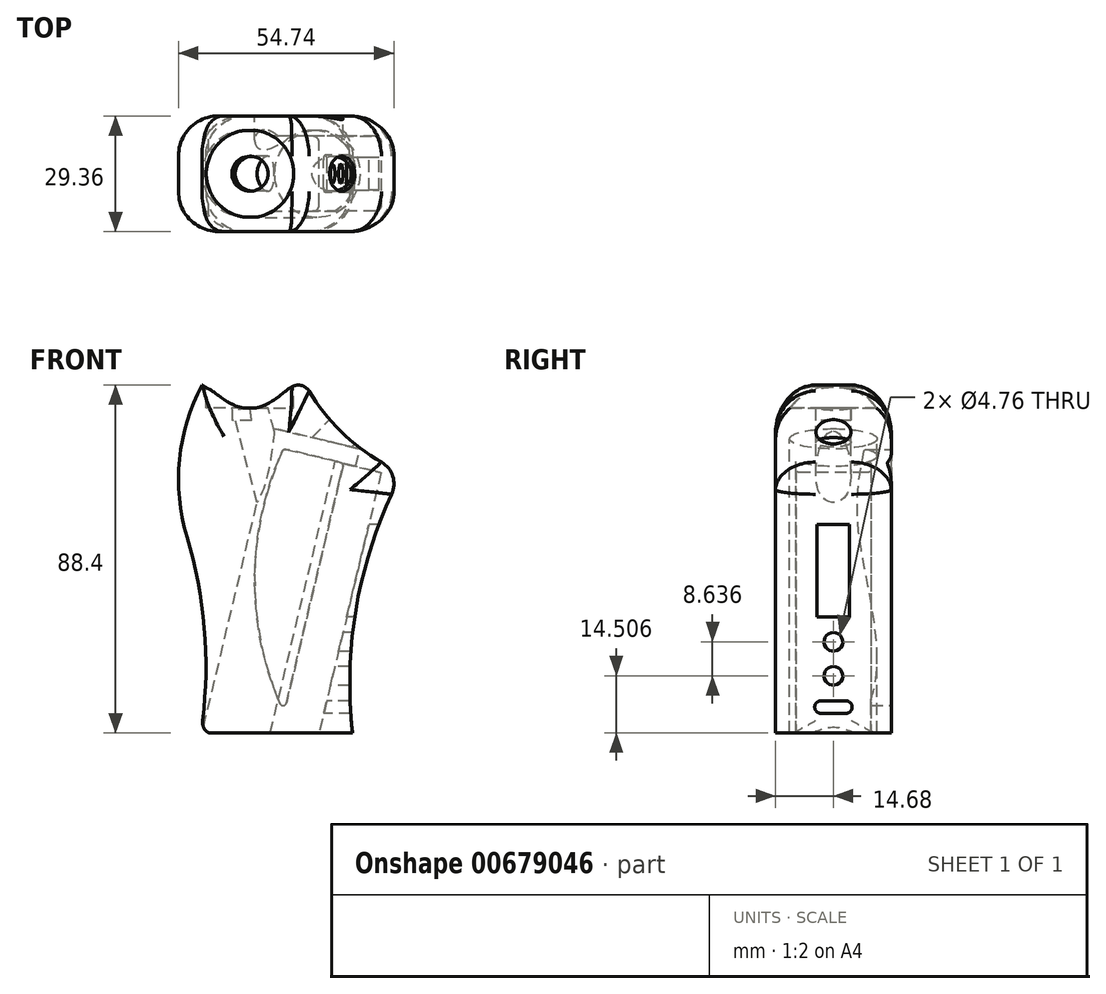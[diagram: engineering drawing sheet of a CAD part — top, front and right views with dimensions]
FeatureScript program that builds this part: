
annotation { "Feature Type Name" : "Feature", "Feature Type Description" : "" }
export const myFeature = defineFeature(function(context is Context, id is Id, definition is map)
    precondition{}
    {
        {
            var Q0;
            Q0=qCreatedBy(makeId("Front.planeOp"),FACE);
            var sketch = newSketch(context, id + "F0", { "sketchPlane" : qUnion([Q0])});
            skLineSegment(sketch, "E0", {"start": v(-23.81, -66.17) * mm, "end": v(12.7, -66.17) * mm});
            skArc(sketch, "E1", {"start": v(22.65, -5.53) * mm, "mid": v(13.52, -35.17) * mm, "end": v(12.7, -66.17) * mm});
            skArc(sketch, "E2", {"start": v(1.68, 20.68) * mm, "mid": v(9.7, 10.49) * mm, "end": v(20.04, 2.66) * mm});
            skArc(sketch, "E3", {"start": v(-25.38, -63.03) * mm, "mid": v(-24.94, -39.47) * mm, "end": v(-29.35, -16.32) * mm});
            skArc(sketch, "E4", {"start": v(-25.5, 22.23) * mm, "mid": v(-31.24, 3.33) * mm, "end": v(-29.35, -16.32) * mm});
            skLineSegment(sketch, "E5", {"start": v(23.15, -3.9) * mm, "end": v(12.7, -66.17) * mm, "construction": true});
            skLineSegment(sketch, "E6", {"start": v(-31.5, 18.67) * mm, "end": v(-31.5, -66.17) * mm, "construction": true});
            skPoint(sketch, "E7.visualSharp", {"position": v(25.4, 0) * mm});
            skArc(sketch, "E7.filletArc", {"start": v(22.65, -5.53) * mm, "mid": v(22.94, -0.93) * mm, "end": v(20.04, 2.66) * mm});
            skLineSegment(sketch, "E8", {"start": v(23.24, 22.23) * mm, "end": v(23.24, -66.17) * mm, "construction": true});
            skLineSegment(sketch, "E9", {"start": v(-33.86, 18.67) * mm, "end": v(-25.13, -66.17) * mm, "construction": true});
            skPoint(sketch, "E10.visualSharp", {"position": v(0, 23.71) * mm});
            skArc(sketch, "E11", {"start": v(-25.5, 22.23) * mm, "mid": v(-14.17, 18.67) * mm, "end": v(-2.7, 21.76) * mm});
            skLineSegment(sketch, "E12", {"start": v(-33.86, 18.67) * mm, "end": v(23.24, 18.67) * mm, "construction": true});
            skArc(sketch, "E13.filletArc", {"start": v(1.68, 20.68) * mm, "mid": v(-0.29, 22.13) * mm, "end": v(-2.7, 21.76) * mm});
            skLineSegment(sketch, "E14", {"start": v(-25.5, 22.23) * mm, "end": v(23.24, 22.23) * mm, "construction": true});
            skArc(sketch, "E15", {"start": v(-25.38, -63.03) * mm, "mid": v(-25.07, -64.83) * mm, "end": v(-23.81, -66.17) * mm});
            skLineSegment(sketch, "E16", {"start": v(-25.4, 18.67) * mm, "end": v(-25.4, -66.17) * mm, "construction": true});
            skLineSegment(sketch, "E17", {"start": v(0.24, 22.23) * mm, "end": v(23.24, -0.17) * mm, "construction": true});
            skSolve(sketch);
        }
        {
            var Q0;
            Q0=makeQuery(id+"F0.imprint","IMPRINT",FACE,{"disambiguationData":[TD([[makeQuery(id+"F0.imprint","IMPRINT",EDGE,{"derivedFrom":sQuery(id+"F0.wireOp",EDGE,"E0")}),1.0]])]});
            extrude(context, id + "F1", {"entities" : qUnion([Q0]), "endBound" : BoundingType.SYMMETRIC, "depth" : 29.37 * mm, "offsetDistance" : 25.4 * mm});
        }
        {
            var Q0;
            Q0=makeQuery(id+"F1.opExtrude","CAP_EDGE",EDGE,{"disambiguationData":[OSD([sQuery(id+"F0.wireOp",EDGE,"8a65d561-aca7-42f6-96eb-58d541bab6f2")])],"isStart":true});
            var Q1;
            Q1=makeQuery(id+"F1.opExtrude","CAP_EDGE",EDGE,{"disambiguationData":[OSD([sQuery(id+"F0.wireOp",EDGE,"E2")])],"isStart":true});
            var Q2;
            Q2=makeQuery(id+"F1.opExtrude","CAP_EDGE",EDGE,{"disambiguationData":[OSD([sQuery(id+"F0.wireOp",EDGE,"E2")])],"isStart":false});
            var Q3;
            Q3=makeQuery(id+"F1.opExtrude","CAP_EDGE",EDGE,{"disambiguationData":[OSD([sQuery(id+"F0.wireOp",EDGE,"E1")])],"isStart":false});
            var Q4;
            Q4=makeQuery(id+"F1.opExtrude","CAP_EDGE",EDGE,{"disambiguationData":[OSD([sQuery(id+"F0.wireOp",EDGE,"E1")])],"isStart":true});
            var Q5;
            Q5=makeQuery(id+"F1.opExtrude","CAP_EDGE",EDGE,{"disambiguationData":[OSD([sQuery(id+"F0.wireOp",EDGE,"E3")])],"isStart":false});
            var Q6;
            Q6=makeQuery(id+"F1.opExtrude","CAP_EDGE",EDGE,{"disambiguationData":[OSD([sQuery(id+"F0.wireOp",EDGE,"E4")])],"isStart":false});
            var Q7;
            Q7=makeQuery(id+"F1.opExtrude","CAP_EDGE",EDGE,{"disambiguationData":[OSD([sQuery(id+"F0.wireOp",EDGE,"E4")])],"isStart":true});
            var Q8;
            Q8=makeQuery(id+"F1.opExtrude","CAP_EDGE",EDGE,{"disambiguationData":[OSD([sQuery(id+"F0.wireOp",EDGE,"E3")])],"isStart":true});
            var Q9;
            Q9=makeQuery(id+"F1.opExtrude","CAP_EDGE",EDGE,{"disambiguationData":[OSD([sQuery(id+"F0.wireOp",EDGE,"8a65d561-aca7-42f6-96eb-58d541bab6f2")])],"isStart":false});
            var Q10;
            Q10=makeQuery(id+"F1.opExtrude","CAP_EDGE",EDGE,{"disambiguationData":[OSD([sQuery(id+"F0.wireOp",EDGE,"E7.filletArc")])],"isStart":false});
            var Q11;
            Q11=makeQuery(id+"F1.opExtrude","CAP_EDGE",EDGE,{"disambiguationData":[OSD([sQuery(id+"F0.wireOp",EDGE,"E7.filletArc")])],"isStart":true});
            fillet(context, id + "F2", {"entities" : qUnion([Q0, Q1, Q2, Q3, Q4, Q5, Q6, Q7, Q8, Q9, Q10, Q11]), "radius" : 10.16 * mm, "tangentPropagation" : true, "allowEdgeOverflow" : false});
        }
        {
            var Q0;
            Q0=qCreatedBy(makeId("Top.planeOp"),FACE);
            cPlane(context, id + "F3", {"entities" : qUnion([Q0]), "cplaneType" : CPlaneType.OFFSET, "offset" : 22.22 * mm, "width" : 152.4 * mm, "height" : 152.4 * mm});
        }
        {
            var Q0;
            Q0=qCreatedBy(id+"F3.planeOp",FACE);
            var sketch = newSketch(context, id + "F4", { "sketchPlane" : qUnion([Q0])});
            skCircle(sketch, "E18", {"center": v(-13.34, 0) * mm, "radius": 11.11 * mm});
            skSolve(sketch);
        }
        {
            var Q0;
            Q0 = qSketchRegion(id + "F4", true);
            extrude(context, id + "F5", {"entities" : qUnion([Q0]), "operationType" : NewBodyOperationType.REMOVE, "oppositeDirection" : true, "depth" : 5.84 * mm, "offsetDistance" : 25.4 * mm});
        }
        {
            var Q0;
            Q0=makeQuery(id+"F1.opExtrude","SWEPT_FACE",FACE,{"disambiguationData":[OSD([sQuery(id+"F0.wireOp",EDGE,"E0")])]});
            var sketch = newSketch(context, id + "F6", { "sketchPlane" : qUnion([Q0])});
            skCircle(sketch, "E19.0", {"center": v(-13.34, 0) * mm, "radius": 11.11 * mm});
            skSolve(sketch);
        }
        {
            var Q0;
            Q0=makeQuery(id+"F1.opExtrude","CAP_FACE",FACE,{"disambiguationData":[OSD([sQuery(id+"F0.wireOp",EDGE,"E0"),sQuery(id+"F0.wireOp",EDGE,"E1"),sQuery(id+"F0.wireOp",EDGE,"E2"),sQuery(id+"F0.wireOp",EDGE,"E3"),sQuery(id+"F0.wireOp",EDGE,"E4"),sQuery(id+"F0.wireOp",EDGE,"E7.filletArc"),sQuery(id+"F0.wireOp",EDGE,"E11"),sQuery(id+"F0.wireOp",EDGE,"E13.filletArc"),sQuery(id+"F0.wireOp",EDGE,"E15")])],"isStart":true});
            var sketch = newSketch(context, id + "F7", { "sketchPlane" : qUnion([Q0])});
            skLineSegment(sketch, "E20", {"start": v(4.06, -58.5) * mm, "end": v(-10.26, 1.52) * mm});
            skLineSegment(sketch, "E21", {"start": v(-9.59, 2.6) * mm, "end": v(4.11, 5.87) * mm});
            skArc(sketch, "E22", {"start": v(5.77, -58.64) * mm, "mid": v(12.13, -26.57) * mm, "end": v(5.15, 5.36) * mm});
            skLineSegment(sketch, "E23", {"start": v(0, 0) * mm, "end": v(0, -91.95) * mm, "construction": true});
            skPoint(sketch, "E24.visualSharp", {"position": v(4.68, -61.09) * mm});
            skArc(sketch, "E24.filletArc", {"start": v(4.06, -58.5) * mm, "mid": v(4.87, -59.18) * mm, "end": v(5.77, -58.64) * mm});
            skPoint(sketch, "E25.visualSharp", {"position": v(-10.46, 2.4) * mm});
            skArc(sketch, "E25.filletArc", {"start": v(-9.59, 2.6) * mm, "mid": v(-10.15, 2.2) * mm, "end": v(-10.26, 1.52) * mm});
            skPoint(sketch, "E26.visualSharp", {"position": v(4.84, 6.05) * mm});
            skArc(sketch, "E26.filletArc", {"start": v(5.15, 5.36) * mm, "mid": v(4.72, 5.8) * mm, "end": v(4.11, 5.87) * mm});
            skArc(sketch, "E27.0", {"start": v(-22.65, -5.53) * mm, "mid": v(-22.94, -0.93) * mm, "end": v(-20.04, 2.66) * mm});
            skSolve(sketch);
        }
        {
            var Q0;
            Q0 = qSketchRegion(id + "F7", true);
            var Q1;
            Q1=qCreatedBy(makeId("Front.planeOp"),FACE);
            extrude(context, id + "F8", {"entities" : qUnion([Q0]), "operationType" : NewBodyOperationType.REMOVE, "endBound" : BoundingType.UP_TO_SURFACE, "oppositeDirection" : true, "depth" : 25.4 * mm, "endBoundEntityFace" : qUnion([Q1]), "offsetDistance" : 25.4 * mm});
        }
        {
            var Q0;
            Q0=makeQuery(id+"F8.boolean.opBoolean","COPY",FACE,{"derivedFrom":makeQuery(id+"F8.opExtrude","SWEPT_FACE",FACE,{"disambiguationData":[OSD([sQuery(id+"F7.wireOp",EDGE,"E21")])]})});
            var sketch = newSketch(context, id + "F9", { "sketchPlane" : qUnion([Q0])});
            skCircle(sketch, "E28", {"center": v(1.68, 0) * mm, "radius": 11.11 * mm});
            skSolve(sketch);
        }
        {
            var Q0;
            Q0 = qSketchRegion(id + "F9", true);
            var Q1;
            Q1=makeQuery(id+"F1.opExtrude","SWEPT_FACE",FACE,{"disambiguationData":[OSD([sQuery(id+"F0.wireOp",EDGE,"E0")])]});
            extrude(context, id + "F10", {"entities" : qUnion([Q0]), "operationType" : NewBodyOperationType.REMOVE, "endBound" : BoundingType.UP_TO_SURFACE, "depth" : 25.4 * mm, "endBoundEntityFace" : qUnion([Q1]), "offsetDistance" : 25.4 * mm, "hasSecondDirection" : true, "secondDirectionOppositeDirection" : true, "secondDirectionDepth" : 4.44 * mm});
        }
        {
            var Q0;
            Q0=makeQuery(id+"F10.boolean.opBoolean","COPY",FACE,{"derivedFrom":makeQuery(id+"F10.opExtrude","CAP_FACE",FACE,{"disambiguationData":[OSD([sQuery(id+"F9.wireOp",EDGE,"E28")])],"isStart":true})});
            cPlane(context, id + "F11", {"entities" : qUnion([Q0]), "cplaneType" : CPlaneType.OFFSET, "offset" : 76.2 * mm, "flipAlignment" : true, "width" : 152.4 * mm, "height" : 152.4 * mm});
        }
        {
            var Q0;
            Q0=qCreatedBy(id+"F11.planeOp",FACE);
            var sketch = newSketch(context, id + "F12", { "sketchPlane" : qUnion([Q0])});
            skLineSegment(sketch, "E29", {"start": v(19.46, -7.94) * mm, "end": v(19.46, 7.94) * mm});
            skLineSegment(sketch, "E30", {"start": v(17.87, 9.53) * mm, "end": v(6.76, 9.53) * mm});
            skLineSegment(sketch, "E31", {"start": v(6.76, 9.53) * mm, "end": v(6.76, -9.52) * mm});
            skLineSegment(sketch, "E32", {"start": v(6.76, -9.52) * mm, "end": v(17.87, -9.52) * mm});
            skArc(sketch, "E33.0", {"start": v(-7.8, 5.8) * mm, "mid": v(12.8, 0) * mm, "end": v(-7.8, -5.8) * mm});
            skPoint(sketch, "E34.visualSharp", {"position": v(19.46, -9.52) * mm});
            skArc(sketch, "E34.filletArc", {"start": v(17.87, -9.52) * mm, "mid": v(19, -9.06) * mm, "end": v(19.46, -7.94) * mm});
            skPoint(sketch, "E35.visualSharp", {"position": v(19.46, 9.53) * mm});
            skArc(sketch, "E35.filletArc", {"start": v(19.46, 7.94) * mm, "mid": v(19, 9.06) * mm, "end": v(17.87, 9.53) * mm});
            skSolve(sketch);
        }
        {
            var Q0;
            Q0 = qSketchRegion(id + "F12", true);
            extrude(context, id + "F13", {"entities" : qUnion([Q0]), "operationType" : NewBodyOperationType.REMOVE, "oppositeDirection" : true, "depth" : 71.63 * mm, "offsetDistance" : 25.4 * mm});
        }
        {
            var Q0;
            Q0=qCreatedBy(makeId("Right.planeOp"),FACE);
            var sketch = newSketch(context, id + "F14", { "sketchPlane" : qUnion([Q0])});
            skLineSegment(sketch, "E36", {"start": v(-3.17, -59.6) * mm, "end": v(3.18, -59.6) * mm, "construction": true});
            skArc(sketch, "E37", {"start": v(-3.17, -58.01) * mm, "mid": v(-4.76, -59.6) * mm, "end": v(-3.17, -61.19) * mm});
            skArc(sketch, "E38", {"start": v(3.18, -61.19) * mm, "mid": v(4.76, -59.6) * mm, "end": v(3.18, -58.01) * mm});
            skLineSegment(sketch, "E39", {"start": v(-3.17, -58.01) * mm, "end": v(3.18, -58.01) * mm});
            skLineSegment(sketch, "E40", {"start": v(3.18, -61.19) * mm, "end": v(-3.17, -61.19) * mm});
            skLineSegment(sketch, "E41.0.0", {"start": v(-5.8, -66.17) * mm, "end": v(-11.11, -66.17) * mm});
            skLineSegment(sketch, "E41.0.2", {"start": v(7.94, -66.17) * mm, "end": v(7.94, -66.17) * mm});
            skLineSegment(sketch, "E41.0.4", {"start": v(11.11, -66.17) * mm, "end": v(5.8, -66.17) * mm});
            skLineSegment(sketch, "E41.0.5", {"start": v(5.8, -66.17) * mm, "end": v(10.54, -66.17) * mm});
            skFitSpline(sketch, "E41.0.6", {"points": [v(10.54, -66.17) * mm, v(11.92, -66.17) * mm, v(13.3, -66.17) * mm, v(14.68, -66.17) * mm]});
            skFitSpline(sketch, "E41.0.8", {"points": [v(14.68, -66.17) * mm, v(11.3, -66.17) * mm, v(7.91, -66.17) * mm, v(4.52, -66.17) * mm]});
            skLineSegment(sketch, "E41.0.9", {"start": v(4.52, -66.17) * mm, "end": v(-4.52, -66.17) * mm});
            skFitSpline(sketch, "E41.0.10", {"points": [v(-4.52, -66.17) * mm, v(-7.91, -66.17) * mm, v(-11.3, -66.17) * mm, v(-14.68, -66.17) * mm]});
            skFitSpline(sketch, "E41.0.12", {"points": [v(-14.68, -66.17) * mm, v(-13.3, -66.17) * mm, v(-11.92, -66.17) * mm, v(-10.54, -66.17) * mm]});
            skLineSegment(sketch, "E41.0.13", {"start": v(-10.54, -66.17) * mm, "end": v(-5.8, -66.17) * mm});
            skLineSegment(sketch, "E42", {"start": v(0, 0) * mm, "end": v(0, -80.2) * mm, "construction": true});
            skCircle(sketch, "E43", {"center": v(0, -51.66) * mm, "radius": 2.38 * mm});
            skCircle(sketch, "E44", {"center": v(0, -43.03) * mm, "radius": 2.38 * mm});
            skLineSegment(sketch, "E45", {"start": v(-4.13, -13.18) * mm, "end": v(-4.13, -36.68) * mm});
            skLineSegment(sketch, "E46", {"start": v(-4.13, -36.68) * mm, "end": v(4.13, -36.68) * mm});
            skLineSegment(sketch, "E47", {"start": v(4.13, -36.68) * mm, "end": v(4.13, -13.18) * mm});
            skLineSegment(sketch, "E48", {"start": v(4.13, -13.18) * mm, "end": v(-4.13, -13.18) * mm});
            skSolve(sketch);
        }
        {
            var Q0;
            Q0 = qSketchRegion(id + "F14", true);
            extrude(context, id + "F15", {"entities" : qUnion([Q0]), "operationType" : NewBodyOperationType.REMOVE, "endBound" : BoundingType.THROUGH_ALL, "depth" : 25.4 * mm, "offsetDistance" : 25.4 * mm});
        }
        {
            var Q0;
            Q0=sQuery(id+"F0.wireOp",EDGE,"E17");
            cPlane(context, id + "F16", {"entities" : qUnion([Q0]), "cplaneType" : CPlaneType.LINE_ANGLE, "offset" : 25.4 * mm, "angle" : 90 * degree, "width" : 152.4 * mm, "height" : 152.4 * mm});
        }
        {
            var Q0;
            Q0=qCreatedBy(id+"F16.planeOp",FACE);
            var sketch = newSketch(context, id + "F17", { "sketchPlane" : qUnion([Q0])});
            skCircle(sketch, "E49", {"center": v(0, 0) * mm, "radius": 4.45 * mm});
            skSolve(sketch);
        }
        {
            var Q0;
            Q0 = qSketchRegion(id + "F17", true);
            extrude(context, id + "F18", {"entities" : qUnion([Q0]), "operationType" : NewBodyOperationType.REMOVE, "oppositeDirection" : true, "depth" : 25.4 * mm, "offsetDistance" : 25.4 * mm});
        }
        {
            var Q0;
            Q0=qCreatedBy(makeId("Front.planeOp"),FACE);
            var sketch = newSketch(context, id + "F19", { "sketchPlane" : qUnion([Q0])});
            skLineSegment(sketch, "E50", {"start": v(14.58, 5.98) * mm, "end": v(13.52, 1.54) * mm});
            skLineSegment(sketch, "E51", {"start": v(-25.13, -64.69) * mm, "end": v(-7.04, 11.14) * mm});
            skLineSegment(sketch, "E52.0.0", {"start": v(4.22, -66.17) * mm, "end": v(20, -0.01) * mm});
            skLineSegment(sketch, "E52.0.1", {"start": v(20, -0.01) * mm, "end": v(10, 2.37) * mm});
            skArc(sketch, "E52.0.2", {"start": v(10.26, 1.52) * mm, "mid": v(10.24, 1.98) * mm, "end": v(10, 2.37) * mm});
            skLineSegment(sketch, "E52.0.3", {"start": v(10.26, 1.52) * mm, "end": v(-4.06, -58.5) * mm});
            skArc(sketch, "E52.0.4", {"start": v(-5.77, -58.64) * mm, "mid": v(-4.87, -59.18) * mm, "end": v(-4.06, -58.5) * mm});
            skArc(sketch, "E52.0.5", {"start": v(-6.16, -57.7) * mm, "mid": v(-5.97, -58.17) * mm, "end": v(-5.77, -58.64) * mm});
            skLineSegment(sketch, "E52.0.6", {"start": v(-6.16, -57.7) * mm, "end": v(-8.18, -66.17) * mm});
            skLineSegment(sketch, "E52.0.7", {"start": v(-8.18, -66.17) * mm, "end": v(4.22, -66.17) * mm});
            skFitSpline(sketch, "E53.0.0", {"points": [v(-15, 16.38) * mm, v(-15.5, 16.47) * mm, v(-16.45, 16.73) * mm, v(-17.55, 17.18) * mm, v(-18.39, 17.6) * mm, v(-19.18, 18.05) * mm, v(-20.1, 18.64) * mm, v(-21.1, 19.35) * mm, v(-22.02, 20.04) * mm, v(-22.82, 20.64) * mm, v(-23.28, 20.94) * mm, v(-23.48, 21.04) * mm]});
            skFitSpline(sketch, "E53.0.2", {"points": [v(-23.48, 21.04) * mm, v(-23.28, 20.94) * mm, v(-22.95, 20.72) * mm, v(-22.42, 20.34) * mm, v(-21.87, 19.93) * mm, v(-21.12, 19.36) * mm, v(-20.1, 18.64) * mm, v(-19, 17.94) * mm, v(-18, 17.4) * mm, v(-17.12, 17) * mm, v(-16.21, 16.66) * mm, v(-15.5, 16.47) * mm, v(-15, 16.38) * mm]});
            skLineSegment(sketch, "E53.0.3", {"start": v(-15, 16.38) * mm, "end": v(-24.45, 16.38) * mm});
            skFitSpline(sketch, "E53.1.0", {"points": [v(-3.19, 21.48) * mm, v(-3.4, 21.36) * mm, v(-3.74, 21.1) * mm, v(-4.28, 20.69) * mm, v(-4.85, 20.23) * mm, v(-5.62, 19.6) * mm, v(-6.67, 18.82) * mm, v(-7.8, 18.06) * mm, v(-8.85, 17.46) * mm, v(-9.76, 17.04) * mm, v(-10.7, 16.68) * mm, v(-11.44, 16.48) * mm, v(-11.96, 16.38) * mm]});
            skLineSegment(sketch, "E53.1.1", {"start": v(-11.96, 16.38) * mm, "end": v(-2.22, 16.38) * mm});
            skFitSpline(sketch, "E53.1.2", {"points": [v(-11.96, 16.38) * mm, v(-11.44, 16.48) * mm, v(-10.45, 16.75) * mm, v(-9.3, 17.24) * mm, v(-8.44, 17.7) * mm, v(-7.62, 18.18) * mm, v(-6.67, 18.82) * mm, v(-5.8, 19.47) * mm, v(-5.16, 19.98) * mm, v(-4.56, 20.47) * mm, v(-4, 20.9) * mm, v(-3.5, 21.27) * mm, v(-3.29, 21.42) * mm, v(-3.19, 21.48) * mm]});
            skArc(sketch, "E53.1.3", {"start": v(-2.7, 21.76) * mm, "mid": v(-2.94, 21.62) * mm, "end": v(-3.19, 21.48) * mm});
            skArc(sketch, "E53.1.5", {"start": v(-2.7, 21.76) * mm, "mid": v(-2.94, 21.62) * mm, "end": v(-3.19, 21.48) * mm});
            skLineSegment(sketch, "E54", {"start": v(-24.45, 16.38) * mm, "end": v(-2.22, 16.38) * mm, "construction": true});
            skLineSegment(sketch, "E55", {"start": v(-13.34, 16.38) * mm, "end": v(-9.34, 1.49) * mm, "construction": true});
            skLineSegment(sketch, "E56", {"start": v(-13.34, 16.38) * mm, "end": v(-14.98, 22.52) * mm, "construction": true});
            skLineSegment(sketch, "E57", {"start": v(-14.98, 22.52) * mm, "end": v(-8.84, 24.16) * mm, "construction": true});
            skSolve(sketch);
        }
        {
            var Q0;
            Q0=sQuery(id+"F19.wireOp",EDGE,"E57");
            cPlane(context, id + "F20", {"entities" : qUnion([Q0]), "cplaneType" : CPlaneType.LINE_ANGLE, "offset" : 25.4 * mm, "angle" : 90 * degree, "width" : 152.4 * mm, "height" : 152.4 * mm});
        }
        {
            var Q0;
            Q0=qCreatedBy(id+"F20.planeOp",FACE);
            var sketch = newSketch(context, id + "F21", { "sketchPlane" : qUnion([Q0])});
            skCircle(sketch, "E58", {"center": v(-8.64, 0) * mm, "radius": 4.45 * mm});
            skEllipticalArc(sketch, "E59.0.0", {"construction": true});
            skFitSpline(sketch, "E59.0.1", {"points": [v(-10.25, -10.99) * mm, v(-9.26, -10.92) * mm, v(-8.28, -10.94) * mm, v(-7.3, -11.03) * mm], "construction": true});
            skEllipticalArc(sketch, "E59.0.2", {"construction": true});
            skFitSpline(sketch, "E59.0.3", {"points": [v(-7.3, 11.03) * mm, v(-8.3, 10.93) * mm, v(-9.28, 10.92) * mm, v(-10.25, 10.99) * mm], "construction": true});
            const initialGuessF21  = {"E59.0.0": [-0.00864038847765013, 0, 0, -1, 0.0111125, 0.010733850744637272, 3.2921964586497707, 6.132581502122209], "E59.0.2": [-0.00864038847765013, 0, 0, -1, 0.0111125, 0.010733850744637272, 0.12439657041784631, 3.0171960831680673]};
            skSetInitialGuess(sketch, initialGuessF21);
            skSolve(sketch);
        }
        {
            var Q0;
            Q0 = qSketchRegion(id + "F21", true);
            var Q1;
            Q1=makeQuery(id+"F10.boolean.opBoolean","COPY",FACE,{"derivedFrom":makeQuery(id+"F10.opExtrude","SWEPT_FACE",FACE,{"disambiguationData":[OSD([sQuery(id+"F9.wireOp",EDGE,"E28")])]})});
            extrude(context, id + "F22", {"entities" : qUnion([Q0]), "operationType" : NewBodyOperationType.REMOVE, "endBound" : BoundingType.UP_TO_SURFACE, "oppositeDirection" : true, "depth" : 25.4 * mm, "endBoundEntityFace" : qUnion([Q1]), "offsetDistance" : 25.4 * mm});
        }
        {
            var Q0;
            Q0=makeQuery(id+"F5.boolean.opBoolean","COPY",FACE,{"derivedFrom":makeQuery(id+"F5.opExtrude","CAP_FACE",FACE,{"disambiguationData":[OSD([sQuery(id+"F4.wireOp",EDGE,"E18")])],"isStart":false})});
            var sketch = newSketch(context, id + "F23", { "sketchPlane" : qUnion([Q0])});
            skArc(sketch, "E60.0.0", {"start": v(-15, 10.99) * mm, "mid": v(-24.45, 0) * mm, "end": v(-15, -10.99) * mm, "construction": true});
            skFitSpline(sketch, "E60.0.1", {"points": [v(-47.9, -5.78) * mm, v(-47.83, -6.22) * mm, v(-47.68, -6.86) * mm, v(-47.38, -7.7) * mm, v(-47.02, -8.51) * mm, v(-46.47, -9.45) * mm, v(-45.79, -10.32) * mm, v(-45.17, -10.96) * mm, v(-44.52, -11.56) * mm, v(-43.82, -12.1) * mm, v(-43.08, -12.57) * mm, v(-42.5, -12.9) * mm, v(-41.91, -13.2) * mm, v(-40.7, -13.72) * mm, v(-39.25, -14.17) * mm, v(-37.52, -14.49) * mm, v(-35.76, -14.68) * mm, v(-34.01, -14.7) * mm, v(-32.26, -14.59) * mm, v(-30.5, -14.4) * mm, v(-28.34, -14.01) * mm, v(-25.78, -13.4) * mm, v(-23.24, -12.7) * mm, v(-21.13, -12.12) * mm, v(-19.43, -11.7) * mm, v(-17.71, -11.31) * mm, v(-15.59, -10.98) * mm, v(-13.08, -10.9) * mm, v(-10.61, -11.15) * mm, v(-8.18, -11.64) * mm, v(-5.76, -12.28) * mm, v(-3.35, -12.95) * mm, v(-0.94, -13.6) * mm, v(1.49, -14.13) * mm, v(3.94, -14.52) * mm, v(5.98, -14.68) * mm, v(7.62, -14.69) * mm, v(8.85, -14.62) * mm, v(10.07, -14.48) * mm, v(11.3, -14.26) * mm, v(12.49, -13.95) * mm, v(13.65, -13.55) * mm, v(14.78, -13.04) * mm, v(15.87, -12.43) * mm, v(16.87, -11.71) * mm, v(17.65, -11.02) * mm, v(18.22, -10.42) * mm, v(18.74, -9.78) * mm, v(19.33, -8.93) * mm, v(19.89, -7.8) * mm, v(20.21, -6.83) * mm, v(20.4, -6.03) * mm, v(20.51, -5.2) * mm, v(20.54, -4.38) * mm, v(20.47, -3.56) * mm, v(20.38, -2.94) * mm, v(20.24, -2.33) * mm, v(20, -1.55) * mm, v(19.67, -0.8) * mm, v(19.28, -0.08) * mm, v(18.82, 0.63) * mm, v(18.18, 1.43) * mm, v(17.3, 2.3) * mm, v(16.32, 3.07) * mm, v(15.28, 3.73) * mm, v(14.18, 4.28) * mm, v(13.03, 4.73) * mm, v(11.84, 5.08) * mm, v(10.63, 5.34) * mm, v(9.41, 5.52) * mm, v(8.17, 5.62) * mm, v(6.94, 5.65) * mm, v(5.31, 5.6) * mm, v(3.3, 5.4) * mm, v(0.93, 4.97) * mm, v(-1.42, 4.42) * mm, v(-3.76, 3.79) * mm, v(-6.1, 3.13) * mm, v(-8.05, 2.63) * mm, v(-9.63, 2.3) * mm, v(-10.82, 2.1) * mm, v(-12.02, 1.96) * mm, v(-13.59, 1.87) * mm, v(-15.53, 1.94) * mm, v(-17.81, 2.27) * mm, v(-20.06, 2.79) * mm, v(-22.3, 3.4) * mm, v(-24.54, 4.02) * mm, v(-26.78, 4.6) * mm, v(-29.04, 5.1) * mm, v(-31.32, 5.46) * mm, v(-33.6, 5.65) * mm, v(-35.5, 5.64) * mm, v(-37.04, 5.5) * mm, v(-38.18, 5.33) * mm, v(-39.3, 5.08) * mm, v(-40.4, 4.76) * mm, v(-41.48, 4.35) * mm, v(-42.53, 3.85) * mm, v(-43.52, 3.26) * mm, v(-44.45, 2.57) * mm, v(-45.31, 1.8) * mm, v(-46.08, 0.92) * mm, v(-46.62, 0.14) * mm, v(-47, -0.54) * mm, v(-47.34, -1.24) * mm, v(-47.67, -2.14) * mm, v(-47.84, -2.89) * mm, v(-47.9, -3.27) * mm], "construction": true});
            skArc(sketch, "E60.0.2", {"start": v(-11.96, -11.03) * mm, "mid": v(-2.22, 0) * mm, "end": v(-11.96, 11.03) * mm, "construction": true});
            skFitSpline(sketch, "E60.0.3", {"points": [v(-47.9, 3.27) * mm, v(-47.83, 2.83) * mm, v(-47.68, 2.18) * mm, v(-47.38, 1.34) * mm, v(-47.02, 0.54) * mm, v(-46.47, -0.4) * mm, v(-45.79, -1.27) * mm, v(-45.17, -1.91) * mm, v(-44.52, -2.5) * mm, v(-43.82, -3.04) * mm, v(-43.08, -3.52) * mm, v(-42.5, -3.85) * mm, v(-41.91, -4.14) * mm, v(-40.7, -4.67) * mm, v(-39.25, -5.12) * mm, v(-37.52, -5.44) * mm, v(-35.76, -5.63) * mm, v(-34.01, -5.66) * mm, v(-32.26, -5.54) * mm, v(-30.5, -5.34) * mm, v(-28.34, -4.96) * mm, v(-25.78, -4.35) * mm, v(-23.24, -3.66) * mm, v(-21.13, -3.07) * mm, v(-19.43, -2.64) * mm, v(-17.71, -2.26) * mm, v(-15.59, -1.93) * mm, v(-13.08, -1.85) * mm, v(-10.61, -2.1) * mm, v(-8.18, -2.6) * mm, v(-5.76, -3.23) * mm, v(-3.35, -3.9) * mm, v(-0.94, -4.54) * mm, v(1.49, -5.08) * mm, v(3.94, -5.48) * mm, v(5.98, -5.64) * mm, v(7.62, -5.64) * mm, v(8.85, -5.58) * mm, v(10.07, -5.44) * mm, v(11.3, -5.21) * mm, v(12.49, -4.9) * mm, v(13.65, -4.5) * mm, v(14.78, -4) * mm, v(15.87, -3.38) * mm, v(16.87, -2.66) * mm, v(17.65, -1.97) * mm, v(18.22, -1.37) * mm, v(18.74, -0.73) * mm, v(19.33, 0.12) * mm, v(19.89, 1.24) * mm, v(20.21, 2.21) * mm, v(20.4, 3.02) * mm, v(20.51, 3.85) * mm, v(20.54, 4.67) * mm, v(20.47, 5.5) * mm, v(20.38, 6.1) * mm, v(20.24, 6.71) * mm, v(20, 7.5) * mm, v(19.67, 8.25) * mm, v(19.28, 8.97) * mm, v(18.82, 9.67) * mm, v(18.18, 10.48) * mm, v(17.3, 11.35) * mm, v(16.32, 12.12) * mm, v(15.28, 12.78) * mm, v(14.18, 13.32) * mm, v(13.03, 13.78) * mm, v(11.84, 14.13) * mm, v(10.63, 14.4) * mm, v(9.41, 14.57) * mm, v(8.17, 14.67) * mm, v(6.94, 14.7) * mm, v(5.31, 14.64) * mm, v(3.3, 14.44) * mm, v(0.93, 14.02) * mm, v(-1.42, 13.47) * mm, v(-3.76, 12.84) * mm, v(-6.1, 12.18) * mm, v(-8.05, 11.68) * mm, v(-9.63, 11.35) * mm, v(-10.82, 11.15) * mm, v(-12.02, 11) * mm, v(-13.59, 10.92) * mm, v(-15.53, 10.98) * mm, v(-17.81, 11.32) * mm, v(-20.06, 11.84) * mm, v(-22.3, 12.44) * mm, v(-24.54, 13.07) * mm, v(-26.78, 13.65) * mm, v(-29.04, 14.14) * mm, v(-31.32, 14.5) * mm, v(-33.6, 14.7) * mm, v(-35.5, 14.69) * mm, v(-37.04, 14.55) * mm, v(-38.18, 14.38) * mm, v(-39.3, 14.13) * mm, v(-40.4, 13.8) * mm, v(-41.48, 13.4) * mm, v(-42.53, 12.9) * mm, v(-43.52, 12.3) * mm, v(-44.45, 11.62) * mm, v(-45.31, 10.84) * mm, v(-46.08, 9.97) * mm, v(-46.62, 9.18) * mm, v(-47, 8.5) * mm, v(-47.34, 7.81) * mm, v(-47.67, 6.91) * mm, v(-47.84, 6.16) * mm, v(-47.9, 5.78) * mm], "construction": true});
            skCircle(sketch, "E61", {"center": v(-13.34, 0) * mm, "radius": 4.45 * mm});
            skSolve(sketch);
        }
        {
            var Q0;
            Q0 = qSketchRegion(id + "F23", true);
            extrude(context, id + "F24", {"entities" : qUnion([Q0]), "operationType" : NewBodyOperationType.REMOVE, "oppositeDirection" : true, "depth" : 3.17 * mm, "offsetDistance" : 25.4 * mm});
        }
    });
